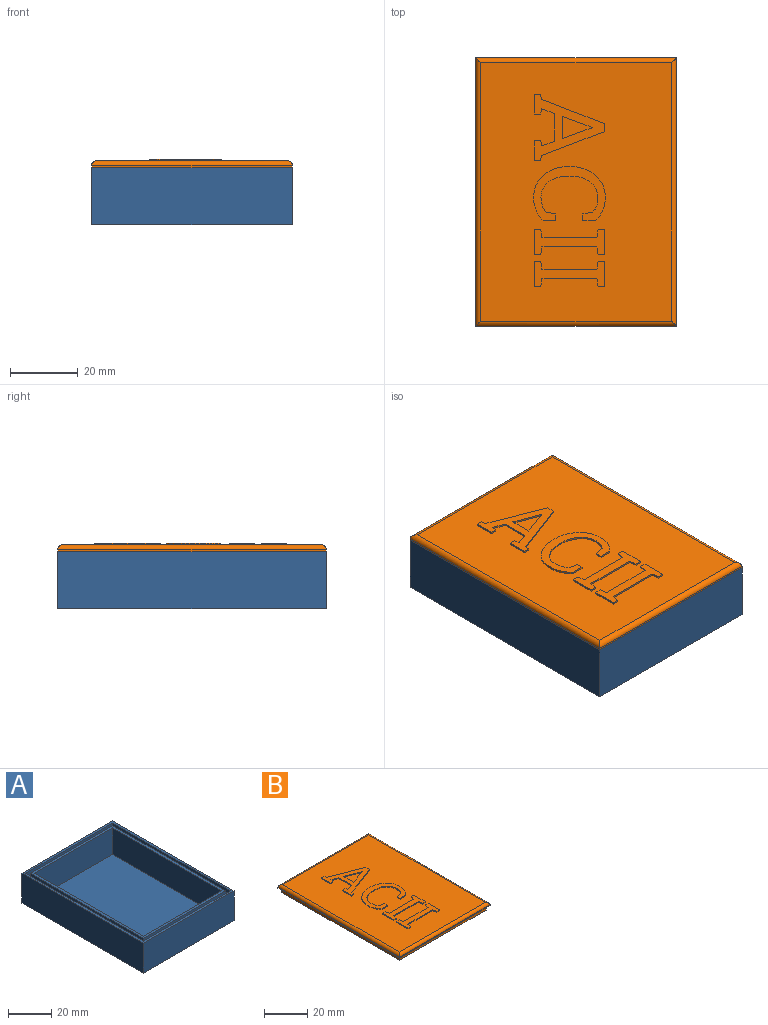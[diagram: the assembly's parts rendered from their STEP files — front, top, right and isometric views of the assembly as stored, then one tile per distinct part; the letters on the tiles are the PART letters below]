
ASSEMBLY  parts=2 mates=1
PART A: 21 faces, bbox 59.5x79.5x17 mm
  f0: plane 74x54mm, normal (0,0,1), area 313.8mm2, adj f1,f2,f3,f4,f9,f10,f11,f12
  f1: plane 71.5x15mm, normal (1,0,0), area 1072.5mm2, adj f0,f2,f4,f5
  f2: plane 51.5x15mm, normal (0,-1,0), area 772.5mm2, adj f0,f1,f3,f5
  f3: plane 71.5x15mm, normal (-1,0,0), area 1072.5mm2, adj f0,f2,f4,f5
  f4: plane 51.5x15mm, normal (0,1,0), area 772.5mm2, adj f0,f1,f3,f5
  f5: plane 71.5x51.5mm, normal (0,0,1), area 3682.2mm2, adj f1,f2,f3,f4
  f6: plane 57x2.5mm, normal (0,-1,0), area 142.5mm2, adj f7,f13,f14,f20
  f7: plane 77x2.5mm, normal (1,0,0), area 192.5mm2, adj f6,f8,f14,f20
  f8: plane 57x2.5mm, normal (0,1,0), area 142.5mm2, adj f7,f13,f14,f20
  f9: plane 74x2.5mm, normal (1,0,0), area 185mm2, adj f0,f10,f12,f14
  f10: plane 54x2.5mm, normal (0,-1,0), area 135mm2, adj f0,f9,f11,f14
  f11: plane 74x2.5mm, normal (-1,0,0), area 185mm2, adj f0,f10,f12,f14
  f12: plane 54x2.5mm, normal (0,1,0), area 135mm2, adj f0,f9,f11,f14
  f13: plane 77x2.5mm, normal (-1,0,0), area 192.5mm2, adj f6,f8,f14,f20
  f14: plane 77x57mm, normal (0,0,1), area 393mm2, adj f6,f7,f8,f9,f10,f11,f12,f13
  f15: plane 79.5x59.5mm, normal (0,0,-1), area 4730.2mm2, adj f16,f17,f18,f19
  f16: plane 59.5x17mm, normal (0,-1,0), area 1011.5mm2, adj f15,f17,f19,f20
  f17: plane 79.5x17mm, normal (-1,0,0), area 1351.5mm2, adj f15,f16,f18,f20
  f18: plane 59.5x17mm, normal (0,1,0), area 1011.5mm2, adj f15,f17,f19,f20
  f19: plane 79.5x17mm, normal (1,0,0), area 1351.5mm2, adj f15,f16,f18,f20
  f20: plane 79.5x59.5mm, normal (0,0,1), area 341.3mm2, adj f6,f7,f8,f13,f16,f17,f18,f19
PART B: 93 faces, bbox 59.5x79.5x4.9 mm
  f0: plane 79.5x59.5mm, normal (0,0,-1), area 341.2mm2, adj f2,f3,f4,f5,f83,f84,f85,f90
  f1: plane 76.5x56.5mm, normal (0,0,1), area 3895.6mm2, adj f9,f10,f11,f12,f13,f14,f15,f16
  f2: plane 59.5x0.5mm, normal (0,1,0), area 29.8mm2, adj f0,f3,f5,f79
  f3: plane 79.5x0.5mm, normal (-1,0,0), area 39.8mm2, adj f0,f2,f4,f80
  f4: plane 59.5x0.5mm, normal (0,-1,0), area 29.8mm2, adj f0,f3,f5,f82
  f5: plane 79.5x0.5mm, normal (1,0,0), area 39.7mm2, adj f0,f2,f4,f81
  f6: plane 6.54x0.5mm, normal (1,0,0), area 3.3mm2, adj f7,f25,f26,f27
  f7: plane 8.85x3.26mm, normal (-0.35,-0.94,0), area 4.7mm2, adj f6,f8,f26,f27
  f8: plane 0.5x0.09mm, normal (-1,0,0), area 0mm2, adj f7,f25,f26,f27
  f9: plane 1.53x0.5mm, normal (0.99,0.14,0), area 0.8mm2, adj f1,f10,f24,f26
  f10: plane 1.78x0.5mm, normal (0,1,0), area 0.9mm2, adj f1,f9,f11,f26
  f11: plane 5.9x0.5mm, normal (-1,0,0), area 3mm2, adj f1,f10,f12,f26
  f12: plane 1.78x0.5mm, normal (0,-1,0), area 0.9mm2, adj f1,f11,f13,f26
  f13: plane 1.56x0.5mm, normal (0.99,-0.17,0), area 0.8mm2, adj f1,f12,f14,f26
  f14: plane 3.8x1.4mm, normal (-0.35,-0.94,0), area 2mm2, adj f1,f13,f15,f26
  f15: plane 8.25x0.5mm, normal (-1,0,0), area 4.1mm2, adj f1,f14,f16,f26
  f16: plane 3.8x1.36mm, normal (-0.34,0.94,0), area 2mm2, adj f1,f15,f17,f26
  f17: plane 1.56x0.5mm, normal (0.99,0.17,0), area 0.8mm2, adj f1,f16,f18,f26
  f18: plane 1.78x0.5mm, normal (0,1,0), area 0.9mm2, adj f1,f17,f19,f26
  f19: plane 5.92x0.5mm, normal (-1,0,0), area 3mm2, adj f1,f18,f20,f26
  f20: plane 1.78x0.5mm, normal (0,-1,0), area 0.9mm2, adj f1,f19,f21,f26
  f21: plane 1.51x0.5mm, normal (0.99,-0.14,0), area 0.8mm2, adj f1,f20,f22,f26
  f22: plane 18.61x7.08mm, normal (0.36,-0.93,0), area 10mm2, adj f1,f21,f23,f26
  f23: plane 2.39x0.5mm, normal (1,0,0), area 1.2mm2, adj f1,f22,f24,f26
  f24: plane 18.61x7.21mm, normal (0.36,0.93,0), area 10mm2, adj f1,f9,f23,f26
  f25: plane 8.85x3.2mm, normal (-0.34,0.94,0), area 4.7mm2, adj f6,f8,f26,f27
  f26: plane 20.61x19.72mm, normal (0,0,1), area 134mm2, adj f6,f7,f8,f9,f10,f11,f12,f13
  f27: plane 8.85x6.54mm, normal (0,0,1), area 29.3mm2, adj f6,f7,f8,f25
  f28: plane 1.97x0.5mm, normal (-1,0,0), area 1mm2, adj f1,f29,f51,f52
  f29: plane 3.67x0.5mm, normal (0,-1,0), area 1.8mm2, adj f1,f28,f30,f52
  f30: extruded ~2.68x2.05mm, area 1.7mm2, adj f1,f29,f31,f52
  f31: extruded ~4.13x0.91mm, area 2.1mm2, adj f1,f30,f32,f52
  f32: extruded ~6.64x2.97mm, area 3.8mm2, adj f1,f31,f33,f52
  f33: extruded ~7.5x2.53mm, area 4mm2, adj f1,f32,f34,f52
  f34: plane 0.5x0.29mm, normal (0,1,0), area 0.1mm2, adj f1,f33,f35,f52
  f35: extruded ~7.48x2.58mm, area 4mm2, adj f1,f34,f36,f52
  f36: extruded ~6.6x2.97mm, area 3.7mm2, adj f1,f35,f37,f52
  f37: extruded ~4.13x0.9mm, area 2.1mm2, adj f1,f36,f38,f52
  f38: extruded ~2.68x2.05mm, area 1.7mm2, adj f1,f37,f39,f52
  f39: plane 3.67x0.5mm, normal (0,-1,0), area 1.8mm2, adj f1,f38,f40,f52
  f40: plane 1.97x0.5mm, normal (1,0,0), area 1mm2, adj f1,f39,f41,f52
  f41: plane 2.92x0.53mm, normal (0.18,0.98,0), area 1.5mm2, adj f1,f40,f42,f52
  f42: extruded ~1.77x1.08mm, area 1mm2, adj f1,f41,f43,f52
  f43: extruded ~2.55x0.5mm, area 1.3mm2, adj f1,f42,f44,f52
  f44: extruded ~4.69x2.34mm, area 2.7mm2, adj f1,f43,f45,f52
  f45: extruded ~5.93x1.69mm, area 3.1mm2, adj f1,f44,f46,f52
  f46: plane 0.5x0.33mm, normal (0,-1,0), area 0.2mm2, adj f1,f45,f47,f52
  f47: extruded ~5.91x1.73mm, area 3.1mm2, adj f1,f46,f48,f52
  f48: extruded ~4.94x2.33mm, area 2.8mm2, adj f1,f47,f49,f52
  f49: extruded ~2.37x0.5mm, area 1.2mm2, adj f1,f48,f50,f52
  f50: extruded ~1.67x1.09mm, area 1mm2, adj f1,f49,f51,f52
  f51: plane 2.92x0.53mm, normal (-0.18,0.98,0), area 1.5mm2, adj f1,f28,f50,f52
  f52: plane 21.21x15.98mm, normal (0,0,1), area 111.6mm2, adj f28,f29,f30,f31,f32,f33,f34,f35
  f53: plane 1.8x0.5mm, normal (0,1,0), area 0.9mm2, adj f1,f54,f64,f65
  f54: plane 2.31x0.5mm, normal (-0.99,0.17,0), area 1.2mm2, adj f1,f53,f55,f65
  f55: plane 16.24x0.5mm, normal (0,1,0), area 8.1mm2, adj f1,f54,f56,f65
  f56: plane 2.31x0.5mm, normal (0.99,0.17,0), area 1.2mm2, adj f1,f55,f57,f65
  f57: plane 1.78x0.5mm, normal (0,1,0), area 0.9mm2, adj f1,f56,f58,f65
  f58: plane 7.4x0.5mm, normal (-1,0,0), area 3.7mm2, adj f1,f57,f59,f65
  f59: plane 1.78x0.5mm, normal (0,-1,0), area 0.9mm2, adj f1,f58,f60,f65
  f60: plane 2.31x0.5mm, normal (0.99,-0.17,0), area 1.2mm2, adj f1,f59,f61,f65
  f61: plane 16.24x0.5mm, normal (0,-1,0), area 8.1mm2, adj f1,f60,f62,f65
  f62: plane 2.31x0.5mm, normal (-0.99,-0.17,0), area 1.2mm2, adj f1,f61,f63,f65
  f63: plane 1.8x0.5mm, normal (0,-1,0), area 0.9mm2, adj f1,f62,f64,f65
  f64: plane 7.4x0.5mm, normal (1,0,0), area 3.7mm2, adj f1,f53,f63,f65
  f65: plane 20.61x7.4mm, normal (0,0,1), area 75.9mm2, adj f53,f54,f55,f56,f57,f58,f59,f60
  f66: plane 1.8x0.5mm, normal (0,1,0), area 0.9mm2, adj f1,f67,f77,f78
  f67: plane 2.31x0.5mm, normal (-0.99,0.17,0), area 1.2mm2, adj f1,f66,f68,f78
  f68: plane 16.24x0.5mm, normal (0,1,0), area 8.1mm2, adj f1,f67,f69,f78
  f69: plane 2.31x0.5mm, normal (0.99,0.17,0), area 1.2mm2, adj f1,f68,f70,f78
  f70: plane 1.78x0.5mm, normal (0,1,0), area 0.9mm2, adj f1,f69,f71,f78
  f71: plane 7.4x0.5mm, normal (-1,0,0), area 3.7mm2, adj f1,f70,f72,f78
  f72: plane 1.78x0.5mm, normal (0,-1,0), area 0.9mm2, adj f1,f71,f73,f78
  f73: plane 2.31x0.5mm, normal (0.99,-0.17,0), area 1.2mm2, adj f1,f72,f74,f78
  f74: plane 16.24x0.5mm, normal (0,-1,0), area 8.1mm2, adj f1,f73,f75,f78
  f75: plane 2.31x0.5mm, normal (-0.99,-0.17,0), area 1.2mm2, adj f1,f74,f76,f78
  f76: plane 1.8x0.5mm, normal (0,-1,0), area 0.9mm2, adj f1,f75,f77,f78
  f77: plane 7.4x0.5mm, normal (1,0,0), area 3.7mm2, adj f1,f66,f76,f78
  f78: plane 20.61x7.4mm, normal (0,0,1), area 75.9mm2, adj f66,f67,f68,f69,f70,f71,f72,f73
  f79: cylinder r=1.5mm len=59.5mm, axis (1,0,0), area 137.6mm2, adj f1,f2,f80,f81
  f80: cylinder r=1.5mm len=79.5mm, axis (0,1,0), area 184.7mm2, adj f1,f3,f79,f82
  f81: cylinder r=1.5mm len=79.5mm, axis (0,-1,0), area 184.7mm2, adj f1,f5,f79,f82
  f82: cylinder r=1.5mm len=59.5mm, axis (-1,0,0), area 137.6mm2, adj f1,f4,f80,f81
  f83: plane 57x2.4mm, normal (0,-1,0), area 136.8mm2, adj f0,f84,f90,f91
  f84: plane 77x2.4mm, normal (1,0,0), area 184.8mm2, adj f0,f83,f85,f91
  f85: plane 57x2.4mm, normal (0,1,0), area 136.8mm2, adj f0,f84,f90,f91
  f86: plane 74x2.4mm, normal (-1,0,0), area 177.6mm2, adj f87,f89,f91,f92
  f87: plane 54x2.4mm, normal (0,1,0), area 129.6mm2, adj f86,f88,f91,f92
  f88: plane 74x2.4mm, normal (1,0,0), area 177.6mm2, adj f87,f89,f91,f92
  f89: plane 54x2.4mm, normal (0,-1,0), area 129.6mm2, adj f86,f88,f91,f92
  f90: plane 77x2.4mm, normal (-1,0,0), area 184.8mm2, adj f0,f83,f85,f91
  f91: plane 77x57mm, normal (0,0,-1), area 393mm2, adj f83,f84,f85,f86,f87,f88,f89,f90
  f92: plane 74x54mm, normal (0,0,-1), area 3996mm2, adj f86,f87,f88,f89
PLACE A t=(-29.75,-39.75,2)mm
PLACE B t=(-25.75,-35.75,17)mm
MATE fastened A.f20 <-> B.f0  axis (0,0,1) through (0,0,17)mm
